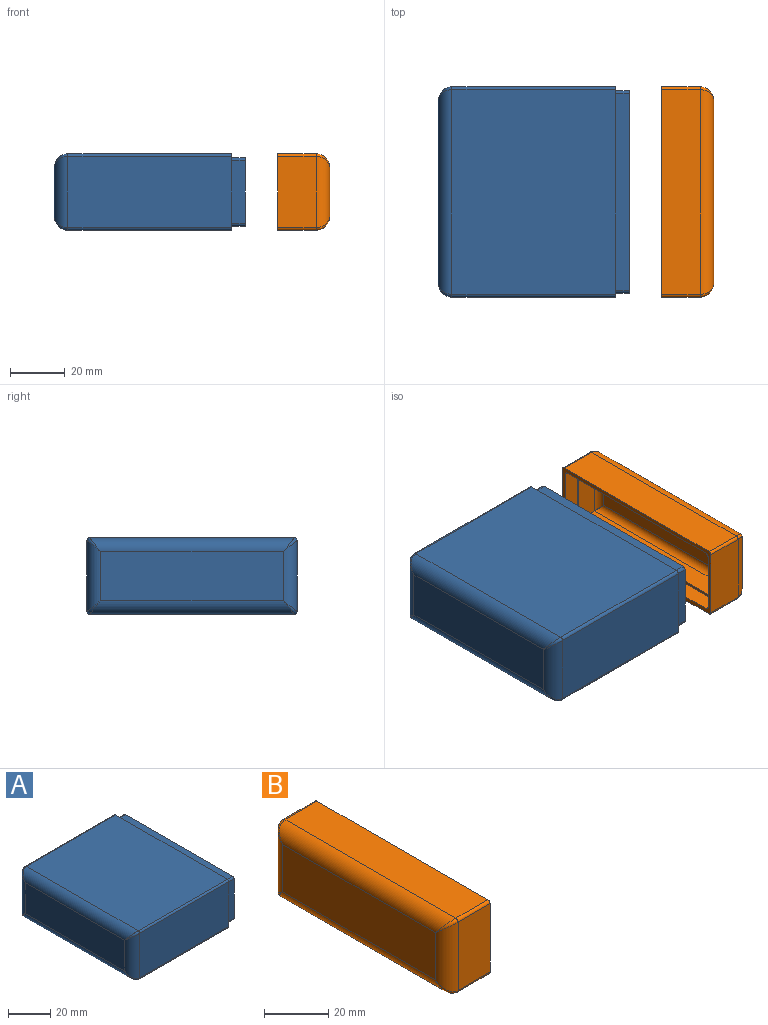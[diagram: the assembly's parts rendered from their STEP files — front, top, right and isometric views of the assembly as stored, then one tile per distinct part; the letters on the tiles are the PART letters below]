
ASSEMBLY  parts=2 mates=2
PART A: 44 faces, bbox 70x77x28 mm
  f0: plane 77x28mm, normal (1,0,0), area 306mm2, adj f1,f3,f4,f5,f6,f7,f8,f9
  f1: plane 60x26mm, normal (0,1,0), area 1560mm2, adj f0,f7,f9,f11
  f2: plane 67x18mm, normal (-1,0,0), area 1206mm2, adj f11,f12,f15,f16
  f3: plane 60x26mm, normal (0,-1,0), area 1560mm2, adj f0,f6,f8,f16
  f4: plane 75x60mm, normal (0,0,1), area 4500mm2, adj f0,f8,f9,f12
  f5: plane 75x60mm, normal (0,0,-1), area 4500mm2, adj f0,f6,f7,f15
  f6: cylinder r=1mm len=60mm, axis (1,0,0), area 94.2mm2, adj f0,f3,f5,f17
  f7: cylinder r=1mm len=60mm, axis (-1,0,0), area 94.2mm2, adj f0,f1,f5,f13
  f8: cylinder r=1mm len=60mm, axis (-1,0,0), area 94.2mm2, adj f0,f3,f4,f14
  f9: cylinder r=1mm len=60mm, axis (1,0,0), area 94.2mm2, adj f0,f1,f4,f10
  f10: bspline ~5.78x5mm, area 8.5mm2, adj f9,f11,f12
  f11: cylinder r=5mm len=26mm, axis (0,0,1), area 181.4mm2, adj f1,f2,f10,f13
  f12: cylinder r=5mm len=75mm, axis (0,1,0), area 566.2mm2, adj f2,f4,f10,f14
  f13: bspline ~5.2x5mm, area 8.5mm2, adj f7,f11,f15
  f14: bspline ~5.2x5mm, area 8.5mm2, adj f8,f12,f16
  f15: cylinder r=5mm len=75mm, axis (0,-1,0), area 566.2mm2, adj f2,f5,f13,f17
  f16: cylinder r=5mm len=26mm, axis (0,0,-1), area 181.4mm2, adj f2,f3,f14,f17
  f17: bspline ~5.78x5mm, area 8.5mm2, adj f6,f15,f16
  f18: plane 23x5mm, normal (0,1,0), area 115mm2, adj f0,f22,f40,f43
  f19: plane 72x5mm, normal (0,0,1), area 360mm2, adj f0,f22,f40,f41
  f20: plane 23x5mm, normal (0,-1,0), area 115mm2, adj f0,f22,f41,f42
  f21: plane 72x5mm, normal (0,0,-1), area 360mm2, adj f0,f22,f42,f43
  f22: plane 74x25mm, normal (1,0,0), area 193.1mm2, adj f18,f19,f20,f21,f35,f37,f38,f39
  f23: plane 67x18mm, normal (1,0,0), area 1206mm2, adj f24,f25,f30,f36
  f24: cylinder r=2.5mm len=23mm, axis (0,0,-1), area 83.2mm2, adj f23,f30,f36,f39
  f25: cylinder r=2.5mm len=23mm, axis (0,0,1), area 83.2mm2, adj f23,f30,f35,f36
  f26: plane 62.45x2mm, normal (0,0,1), area 124.9mm2, adj f27,f28,f29,f30
  f27: plane 62.45x2mm, normal (0,-1,0), area 123.7mm2, adj f26,f28,f30,f37
  f28: plane 2x2mm, normal (1,0,0), area 4mm2, adj f26,f27,f29,f37
  f29: plane 62.45x2mm, normal (0,1,0), area 123.7mm2, adj f26,f28,f30,f37
  f30: cylinder r=2.5mm len=72mm, axis (0,-1,0), area 268.8mm2, adj f23,f24,f25,f26,f27,f29,f37
  f31: plane 62.45x2mm, normal (0,0,-1), area 124.9mm2, adj f32,f33,f34,f36
  f32: plane 62.45x2mm, normal (0,1,0), area 123.7mm2, adj f31,f33,f36,f38
  f33: plane 2x2mm, normal (1,0,0), area 4mm2, adj f31,f32,f34,f38
  f34: plane 62.45x2mm, normal (0,-1,0), area 123.7mm2, adj f31,f33,f36,f38
  f35: plane 65x23mm, normal (0,-1,0), area 1495mm2, adj f22,f25,f37,f38
  f36: cylinder r=2.5mm len=72mm, axis (0,1,0), area 268.8mm2, adj f23,f24,f25,f31,f32,f34,f38
  f37: plane 72x65mm, normal (0,0,1), area 4560mm2, adj f22,f27,f28,f29,f30,f35,f39
  f38: plane 72x65mm, normal (0,0,-1), area 4560mm2, adj f22,f32,f33,f34,f35,f36,f39
  f39: plane 65x23mm, normal (0,1,0), area 1495mm2, adj f22,f24,f37,f38
  f40: cylinder r=1mm len=5mm, axis (-1,0,0), area 7.9mm2, adj f0,f18,f19,f22
  f41: cylinder r=1mm len=5mm, axis (1,0,0), area 7.9mm2, adj f0,f19,f20,f22
  f42: cylinder r=1mm len=5mm, axis (-1,0,0), area 7.9mm2, adj f0,f20,f21,f22
  f43: cylinder r=1mm len=5mm, axis (1,0,0), area 7.9mm2, adj f0,f18,f21,f22
PART B: 36 faces, bbox 19x77x28 mm
  f0: plane 77x28mm, normal (1,0,0), area 315.9mm2, adj f1,f3,f4,f5,f6,f7,f8,f9
  f1: plane 26x14mm, normal (0,1,0), area 364mm2, adj f0,f7,f9,f11
  f2: plane 67x18mm, normal (-1,0,0), area 1206mm2, adj f11,f12,f15,f16
  f3: plane 26x14mm, normal (0,-1,0), area 364mm2, adj f0,f6,f8,f16
  f4: plane 75x14mm, normal (0,0,1), area 1050mm2, adj f0,f8,f9,f12
  f5: plane 75x14mm, normal (0,0,-1), area 1050mm2, adj f0,f6,f7,f15
  f6: cylinder r=1mm len=14mm, axis (1,0,0), area 22mm2, adj f0,f3,f5,f17
  f7: cylinder r=1mm len=14mm, axis (-1,0,0), area 22mm2, adj f0,f1,f5,f13
  f8: cylinder r=1mm len=14mm, axis (-1,0,0), area 22mm2, adj f0,f3,f4,f14
  f9: cylinder r=1mm len=14mm, axis (1,0,0), area 22mm2, adj f0,f1,f4,f10
  f10: bspline ~5.78x5mm, area 8.5mm2, adj f9,f11,f12
  f11: cylinder r=5mm len=26mm, axis (0,0,1), area 181.4mm2, adj f1,f2,f10,f13
  f12: cylinder r=5mm len=75mm, axis (0,1,0), area 566.2mm2, adj f2,f4,f10,f14
  f13: bspline ~5.2x5mm, area 8.5mm2, adj f7,f11,f15
  f14: bspline ~5.2x5mm, area 8.5mm2, adj f8,f12,f16
  f15: cylinder r=5mm len=75mm, axis (0,-1,0), area 566.2mm2, adj f2,f5,f13,f17
  f16: cylinder r=5mm len=26mm, axis (0,0,-1), area 181.4mm2, adj f2,f3,f14,f17
  f17: bspline ~5.78x5mm, area 8.5mm2, adj f6,f15,f16
  f18: plane 22.9x6mm, normal (0,-1,0), area 137.4mm2, adj f0,f22,f32,f35
  f19: plane 71.9x6mm, normal (0,0,-1), area 431.4mm2, adj f0,f22,f32,f33
  f20: plane 22.9x6mm, normal (0,1,0), area 137.4mm2, adj f0,f22,f33,f34
  f21: plane 71.9x6mm, normal (0,0,1), area 431.4mm2, adj f0,f22,f34,f35
  f22: plane 73.9x24.9mm, normal (1,0,0), area 183.3mm2, adj f18,f19,f20,f21,f28,f29,f30,f31
  f23: plane 67x18mm, normal (1,0,0), area 1206mm2, adj f24,f25,f26,f27
  f24: cylinder r=2.5mm len=23mm, axis (0,0,1), area 83.2mm2, adj f23,f26,f27,f31
  f25: cylinder r=2.5mm len=23mm, axis (0,0,-1), area 83.2mm2, adj f23,f26,f27,f30
  f26: cylinder r=2.5mm len=72mm, axis (0,1,0), area 275.6mm2, adj f23,f24,f25,f29
  f27: cylinder r=2.5mm len=72mm, axis (0,-1,0), area 275.6mm2, adj f23,f24,f25,f28
  f28: plane 72x8mm, normal (0,0,1), area 576mm2, adj f22,f27,f30,f31
  f29: plane 72x8mm, normal (0,0,-1), area 576mm2, adj f22,f26,f30,f31
  f30: plane 23x8mm, normal (0,1,0), area 184mm2, adj f22,f25,f28,f29
  f31: plane 23x8mm, normal (0,-1,0), area 184mm2, adj f22,f24,f28,f29
  f32: cylinder r=1mm len=6mm, axis (-1,0,0), area 9.4mm2, adj f0,f18,f19,f22
  f33: cylinder r=1mm len=6mm, axis (1,0,0), area 9.4mm2, adj f0,f19,f20,f22
  f34: cylinder r=1mm len=6mm, axis (-1,0,0), area 9.4mm2, adj f0,f20,f21,f22
  f35: cylinder r=1mm len=6mm, axis (1,0,0), area 9.4mm2, adj f0,f18,f21,f22
PLACE A rot(axis=(0,0,1),0deg) t=(-1.04,3.42,16.18)mm
PLACE B rot(axis=(0,0,-1),180deg) t=(57.9,3.42,16.18)mm
MATE planar A.f3 <-> B.f1  axis (0,-1,0) through (1.46,-35.08,16.18)mm
MATE planar A.f4 <-> B.f4  axis (0,0,1) through (1.46,3.42,30.18)mm
